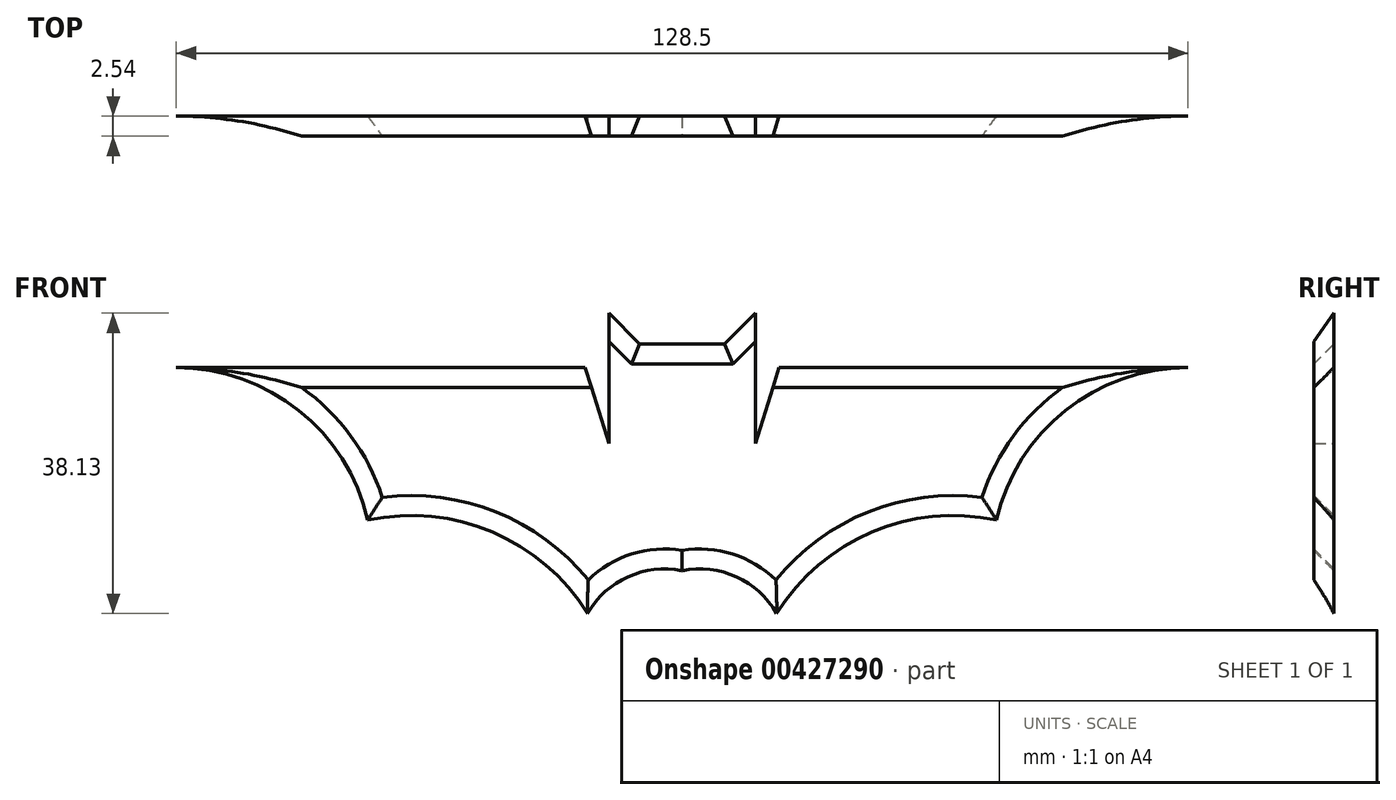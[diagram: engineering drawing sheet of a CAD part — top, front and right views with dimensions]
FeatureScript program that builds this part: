
annotation { "Feature Type Name" : "Feature", "Feature Type Description" : "" }
export const myFeature = defineFeature(function(context is Context, id is Id, definition is map)
    precondition{}
    {
        {
            var Q0;
            Q0=qCreatedBy(makeId("Front.planeOp"),FACE);
            var sketch = newSketch(context, id + "F0", { "sketchPlane" : qUnion([Q0])});
            skLineSegment(sketch, "E0", {"start": v(-64.25, 19.36) * mm, "end": v(-12.3, 19.36) * mm});
            skLineSegment(sketch, "E1", {"start": v(-12.3, 19.36) * mm, "end": v(-9.3, 9.76) * mm});
            skLineSegment(sketch, "E2", {"start": v(-9.3, 9.76) * mm, "end": v(-9.3, 26.27) * mm});
            skLineSegment(sketch, "E3", {"start": v(-9.3, 26.27) * mm, "end": v(-5.4, 22.37) * mm});
            skLineSegment(sketch, "E4", {"start": v(-5.4, 22.37) * mm, "end": v(0, 22.37) * mm});
            skArc(sketch, "E5", {"start": v(-39.93, 0) * mm, "mid": v(-48.7, 13.93) * mm, "end": v(-64.25, 19.36) * mm});
            skArc(sketch, "E6", {"start": v(-12, -11.86) * mm, "mid": v(-24.1, -1.53) * mm, "end": v(-39.93, 0) * mm});
            skArc(sketch, "E7", {"start": v(0, -6.45) * mm, "mid": v(-6.88, -7.2) * mm, "end": v(-12, -11.86) * mm});
            skLineSegment(sketch, "E8", {"start": v(0, 0) * mm, "end": v(0, 58.1) * mm, "construction": true});
            skLineSegment(sketch, "E9.MirrorCS", {"start": v(5.4, 22.37) * mm, "end": v(0, 22.37) * mm});
            skLineSegment(sketch, "E10.MirrorCS", {"start": v(9.3, 26.27) * mm, "end": v(5.4, 22.37) * mm});
            skLineSegment(sketch, "E11.MirrorCS", {"start": v(9.3, 9.76) * mm, "end": v(9.3, 26.27) * mm});
            skLineSegment(sketch, "E12.MirrorCS", {"start": v(12.3, 19.36) * mm, "end": v(9.3, 9.76) * mm});
            skLineSegment(sketch, "E13.MirrorCS", {"start": v(64.25, 19.36) * mm, "end": v(12.3, 19.36) * mm});
            skArc(sketch, "E14.MirrorCS", {"start": v(39.93, 0) * mm, "mid": v(48.7, 13.93) * mm, "end": v(64.25, 19.36) * mm});
            skArc(sketch, "E15.MirrorCS", {"start": v(12, -11.86) * mm, "mid": v(24.1, -1.53) * mm, "end": v(39.93, 0) * mm});
            skArc(sketch, "E16.MirrorCS", {"start": v(0, -6.45) * mm, "mid": v(6.88, -7.2) * mm, "end": v(12, -11.86) * mm});
            skSolve(sketch);
        }
        {
            var Q0;
            Q0=makeQuery(id+"F0.imprint","IMPRINT",FACE,{"disambiguationData":[TD([[makeQuery(id+"F0.imprint","IMPRINT",EDGE,{"derivedFrom":sQuery(id+"F0.wireOp",EDGE,"E0")}),-1.0]])]});
            extrude(context, id + "F1", {"entities" : qUnion([Q0]), "depth" : 2.54 * mm});
        }
        {
            var Q0;
            Q0=makeQuery(id+"F1.opExtrude","CAP_EDGE",EDGE,{"disambiguationData":[OSD([sQuery(id+"F0.wireOp",EDGE,"E0")])],"isStart":false});
            var Q1;
            Q1=makeQuery(id+"F1.opExtrude","CAP_EDGE",EDGE,{"disambiguationData":[OSD([sQuery(id+"F0.wireOp",EDGE,"E13.MirrorCS")])],"isStart":false});
            var Q2;
            Q2=makeQuery(id+"F1.opExtrude","CAP_EDGE",EDGE,{"disambiguationData":[OSD([sQuery(id+"F0.wireOp",EDGE,"E14.MirrorCS")])],"isStart":false});
            var Q3;
            Q3=makeQuery(id+"F1.opExtrude","CAP_EDGE",EDGE,{"disambiguationData":[OSD([sQuery(id+"F0.wireOp",EDGE,"E15.MirrorCS")])],"isStart":false});
            var Q4;
            Q4=makeQuery(id+"F1.opExtrude","CAP_EDGE",EDGE,{"disambiguationData":[OSD([sQuery(id+"F0.wireOp",EDGE,"E16.MirrorCS")])],"isStart":false});
            var Q5;
            Q5=makeQuery(id+"F1.opExtrude","CAP_EDGE",EDGE,{"disambiguationData":[OSD([sQuery(id+"F0.wireOp",EDGE,"E7")])],"isStart":false});
            var Q6;
            Q6=makeQuery(id+"F1.opExtrude","CAP_EDGE",EDGE,{"disambiguationData":[OSD([sQuery(id+"F0.wireOp",EDGE,"E6")])],"isStart":false});
            var Q7;
            Q7=makeQuery(id+"F1.opExtrude","CAP_EDGE",EDGE,{"disambiguationData":[OSD([sQuery(id+"F0.wireOp",EDGE,"E5")])],"isStart":false});
            var Q8;
            Q8=makeQuery(id+"F1.opExtrude","CAP_EDGE",EDGE,{"disambiguationData":[OSD([sQuery(id+"F0.wireOp",EDGE,"E3")])],"isStart":false});
            var Q9;
            Q9=makeQuery(id+"F1.opExtrude","CAP_EDGE",EDGE,{"disambiguationData":[OSD([sQuery(id+"F0.wireOp",EDGE,"E4"),sQuery(id+"F0.wireOp",EDGE,"E9.MirrorCS")])],"isStart":false});
            var Q10;
            Q10=makeQuery(id+"F1.opExtrude","CAP_EDGE",EDGE,{"disambiguationData":[OSD([sQuery(id+"F0.wireOp",EDGE,"E10.MirrorCS")])],"isStart":false});
            chamfer(context, id + "F2", {"entities" : qUnion([Q0, Q1, Q2, Q3, Q4, Q5, Q6, Q7, Q8, Q9, Q10]), "width" : 2.54 * mm, "tangentPropagation" : true});
        }
    });
